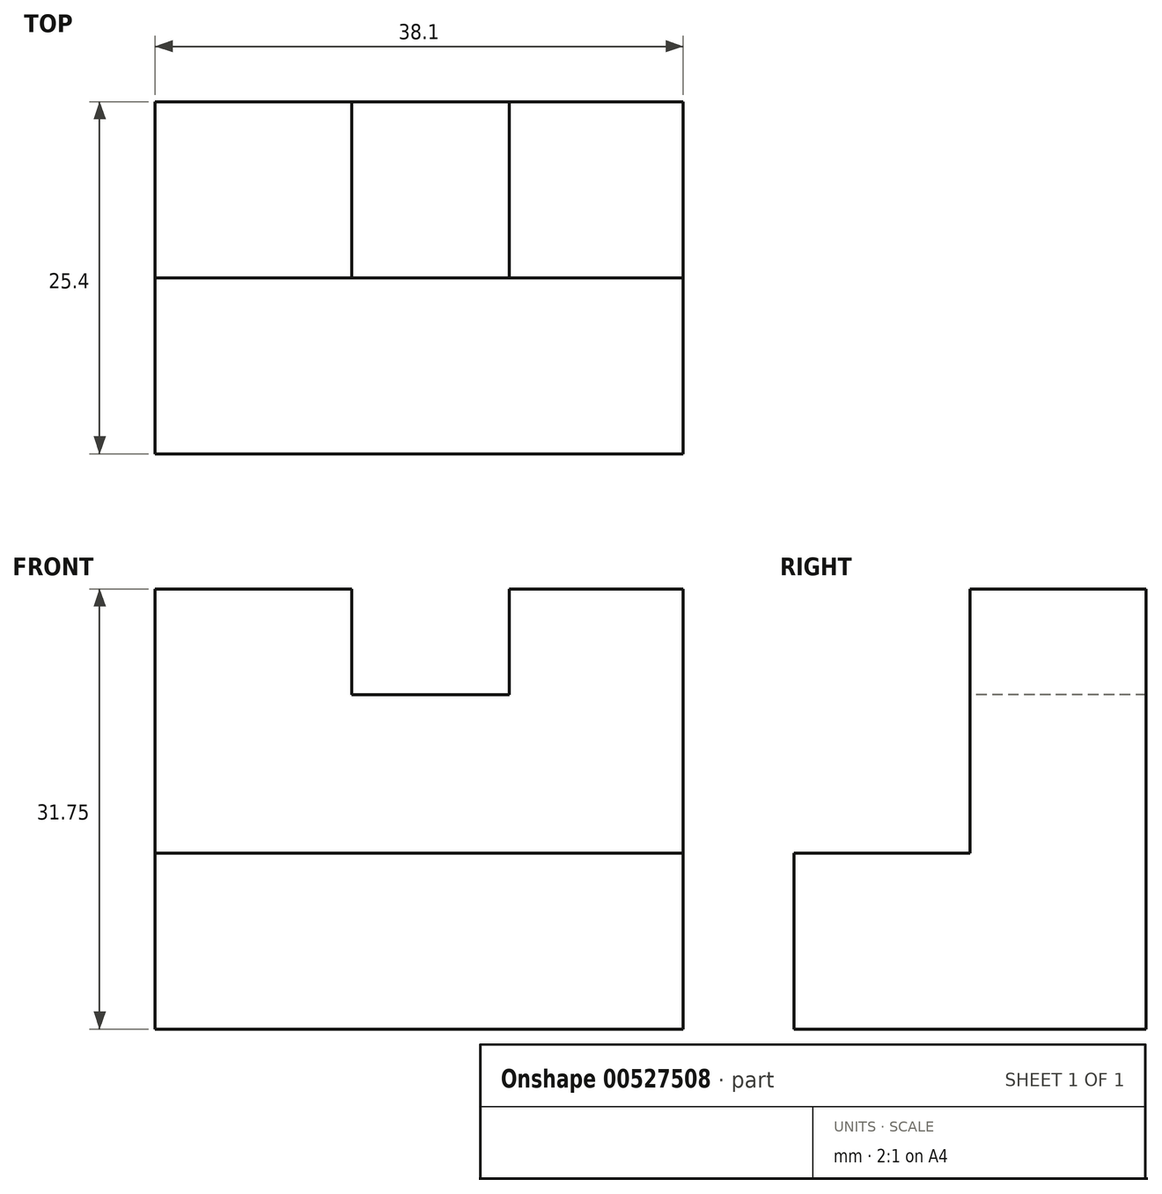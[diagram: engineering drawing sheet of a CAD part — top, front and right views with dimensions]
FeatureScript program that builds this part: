
annotation { "Feature Type Name" : "Feature", "Feature Type Description" : "" }
export const myFeature = defineFeature(function(context is Context, id is Id, definition is map)
    precondition{}
    {
        {
            var Q0;
            Q0=qCreatedBy(makeId("Right.planeOp"),FACE);
            var sketch = newSketch(context, id + "F0", { "sketchPlane" : qUnion([Q0])});
            skLineSegment(sketch, "E0", {"start": v(0, 0) * mm, "end": v(25.4, 0) * mm});
            skLineSegment(sketch, "E1", {"start": v(25.4, 0) * mm, "end": v(25.4, 31.75) * mm});
            skLineSegment(sketch, "E2", {"start": v(25.4, 31.75) * mm, "end": v(12.7, 31.75) * mm});
            skLineSegment(sketch, "E3", {"start": v(12.7, 31.75) * mm, "end": v(12.7, 12.7) * mm});
            skLineSegment(sketch, "E4", {"start": v(12.7, 12.7) * mm, "end": v(0, 12.7) * mm});
            skLineSegment(sketch, "E5", {"start": v(0, 12.7) * mm, "end": v(0, 0) * mm});
            skSolve(sketch);
        }
        {
            var Q0;
            Q0=makeQuery(id+"F0.imprint","IMPRINT",FACE,{"disambiguationData":[TD([[makeQuery(id+"F0.imprint","IMPRINT",EDGE,{"derivedFrom":sQuery(id+"F0.wireOp",EDGE,"E0")}),1.0]])]});
            extrude(context, id + "F1", {"entities" : qUnion([Q0]), "depth" : 38.1 * mm, "offsetDistance" : 25.4 * mm});
        }
        {
            var Q0;
            Q0=makeQuery(id+"F1.opExtrude","SWEPT_FACE",FACE,{"disambiguationData":[OSD([sQuery(id+"F0.wireOp",EDGE,"E3")])]});
            var sketch = newSketch(context, id + "F2", { "sketchPlane" : qUnion([Q0])});
            skLineSegment(sketch, "E6", {"start": v(14.19, 31.75) * mm, "end": v(14.19, 24.12) * mm});
            skLineSegment(sketch, "E7", {"start": v(14.19, 24.12) * mm, "end": v(25.54, 24.12) * mm});
            skLineSegment(sketch, "E8", {"start": v(25.54, 24.12) * mm, "end": v(25.54, 31.75) * mm});
            skSolve(sketch);
        }
        {
            var Q0;
            {var subQ0=sQuery(id+"F2.wireOp",EDGE,"E6");Q0=makeQuery(id+"F2.imprint","IMPRINT",FACE,{"disambiguationData":[TD([[makeQuery(id+"F2.imprint","IMPRINT",EDGE,{"derivedFrom":subQ0}),1.0]])]});}
            extrude(context, id + "F3", {"entities" : qUnion([Q0]), "operationType" : NewBodyOperationType.REMOVE, "oppositeDirection" : true, "depth" : 6.35 * mm, "offsetDistance" : 25.4 * mm});
        }
        {
            var Q0;
            Q0=makeQuery(id+"F3.boolean.opBoolean","COPY",FACE,{"derivedFrom":makeQuery(id+"F3.opExtrude","CAP_FACE",FACE,{"disambiguationData":[OSD([sQuery(id+"F0.wireOp",EDGE,"E2"),sQuery(id+"F0.wireOp",EDGE,"E3"),sQuery(id+"F2.wireOp",EDGE,"E6"),sQuery(id+"F2.wireOp",EDGE,"E7"),sQuery(id+"F2.wireOp",EDGE,"E8")])],"isStart":false})});
            extrude(context, id + "F4", {"entities" : qUnion([Q0]), "operationType" : NewBodyOperationType.REMOVE, "oppositeDirection" : true, "depth" : 12.7 * mm, "offsetDistance" : 25.4 * mm});
        }
    });
